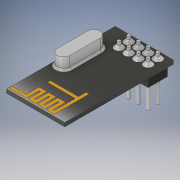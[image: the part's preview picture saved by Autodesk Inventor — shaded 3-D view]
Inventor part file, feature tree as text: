
AUTODESK INVENTOR PART (.ipt)
format: ipt  version: 2019.2 (Build 232265000, 265)  size: 290,816 bytes
history: native  units: mm
features: extrude x5, chamfer x2, emboss x2, fillet x1
ambient origin geometry x8: Origin, YZ Plane, XZ Plane, XY Plane, X Axis, Y Axis, Z Axis, Center Point
bodies: Solid1 (feature_tree)
feature tree (10):
  extrude  "Extrusion1"  Depth=28.0mm
  extrude  "Extrusion2"  Depth=15.0mm
  fillet  "Fillet1"  Radius=11.0mm
  extrude  "Extrusion5"  Depth=3.2mm
  chamfer  "Chamfer2"  Distance=0.5mm
  extrude  "Extrusion3"  Depth=6.0mm
  chamfer  "Chamfer1"  Distance=10.0mm
  extrude  "Extrusion4"  Depth=5.0mm
  emboss  "Emboss2"
  emboss  "Emboss1"
